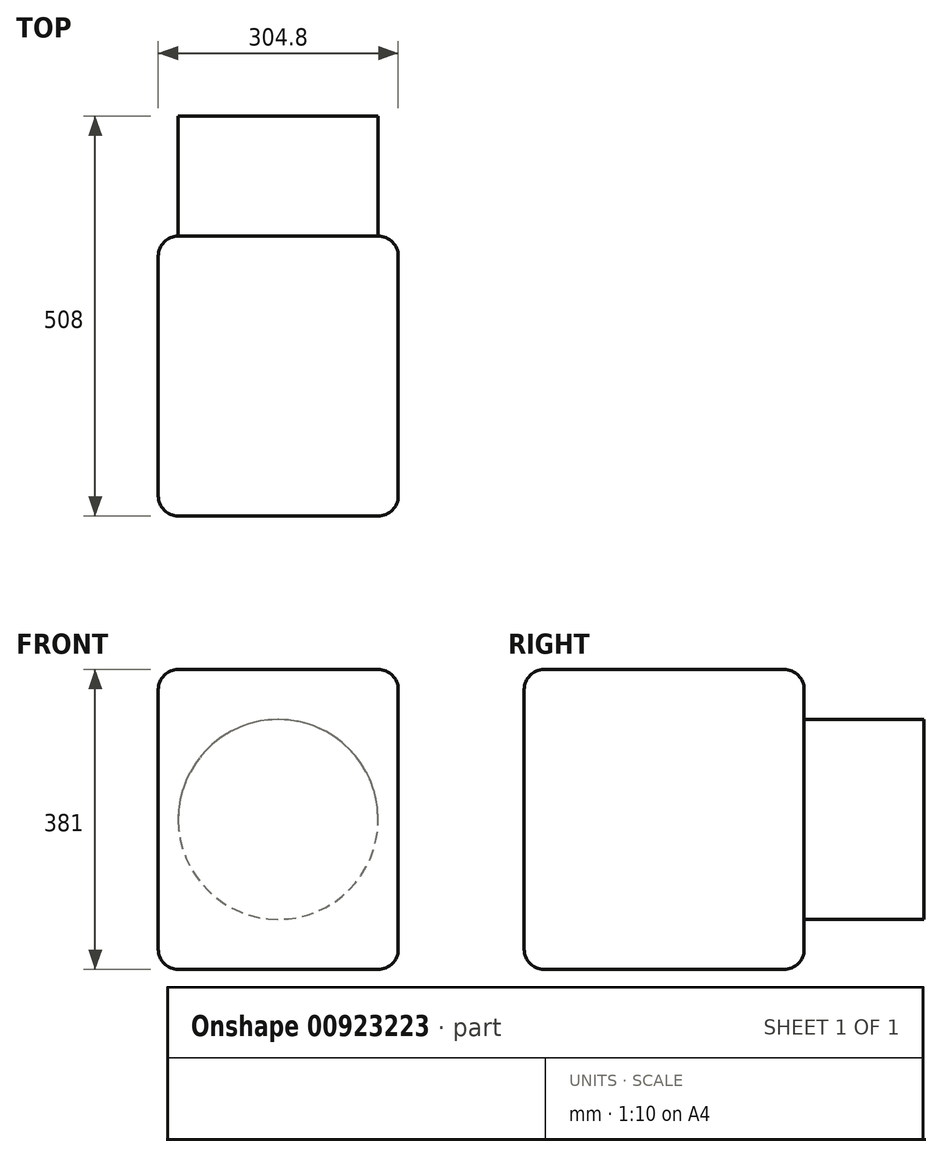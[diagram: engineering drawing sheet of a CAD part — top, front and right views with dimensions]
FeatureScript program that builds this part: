
annotation { "Feature Type Name" : "Feature", "Feature Type Description" : "" }
export const myFeature = defineFeature(function(context is Context, id is Id, definition is map)
    precondition{}
    {
        {
            var Q0;
            Q0=qCreatedBy(makeId("Front.planeOp"),FACE);
            var sketch = newSketch(context, id + "F0", { "sketchPlane" : qUnion([Q0])});
            skLineSegment(sketch, "E0.bottom", {"start": v(152.4, 190.5) * mm, "end": v(-152.4, 190.5) * mm});
            skLineSegment(sketch, "E0.top", {"start": v(152.4, -190.5) * mm, "end": v(-152.4, -190.5) * mm});
            skLineSegment(sketch, "E0.left", {"start": v(152.4, 190.5) * mm, "end": v(152.4, -190.5) * mm});
            skLineSegment(sketch, "E0.right", {"start": v(-152.4, 190.5) * mm, "end": v(-152.4, -190.5) * mm});
            skPoint(sketch, "E0.middle", {"position": v(0, 0) * mm});
            skSolve(sketch);
        }
        {
            var Q0;
            Q0=qSketchRegion(id+"F0",true);
            extrude(context, id + "F1", {"entities" : qUnion([Q0]), "offsetDistance" : 25.4 * mm, "depth" : 355.6 * mm});
        }
        {
            var Q0;
            Q0=makeQuery(id+"F1.opExtrude","CAP_EDGE",EDGE,{"disambiguationData":[OSD([sQuery(id+"F0.wireOp",EDGE,"E0.right")])],"isStart":false});
            var Q1;
            Q1=makeQuery(id+"F1.opExtrude","CAP_EDGE",EDGE,{"disambiguationData":[OSD([sQuery(id+"F0.wireOp",EDGE,"E0.bottom")])],"isStart":false});
            var Q2;
            Q2=makeQuery(id+"F1.opExtrude","CAP_EDGE",EDGE,{"disambiguationData":[OSD([sQuery(id+"F0.wireOp",EDGE,"E0.left")])],"isStart":false});
            var Q3;
            Q3=makeQuery(id+"F1.opExtrude","CAP_EDGE",EDGE,{"disambiguationData":[OSD([sQuery(id+"F0.wireOp",EDGE,"E0.top")])],"isStart":false});
            var Q4;
            Q4=makeQuery(id+"F1.opExtrude","SWEPT_EDGE",EDGE,{"disambiguationData":[OSD([sQuery(id+"F0.wireOp",EDGE,"E0.top"),sQuery(id+"F0.wireOp",EDGE,"E0.right")])]});
            var Q5;
            Q5=makeQuery(id+"F1.opExtrude","SWEPT_EDGE",EDGE,{"disambiguationData":[OSD([sQuery(id+"F0.wireOp",EDGE,"E0.bottom"),sQuery(id+"F0.wireOp",EDGE,"E0.right")])]});
            var Q6;
            Q6=makeQuery(id+"F1.opExtrude","SWEPT_EDGE",EDGE,{"disambiguationData":[OSD([sQuery(id+"F0.wireOp",EDGE,"E0.bottom"),sQuery(id+"F0.wireOp",EDGE,"E0.left")])]});
            var Q7;
            Q7=makeQuery(id+"F1.opExtrude","SWEPT_EDGE",EDGE,{"disambiguationData":[OSD([sQuery(id+"F0.wireOp",EDGE,"E0.top"),sQuery(id+"F0.wireOp",EDGE,"E0.left")])]});
            var Q8;
            Q8=makeQuery(id+"F1.opExtrude","CAP_EDGE",EDGE,{"disambiguationData":[OSD([sQuery(id+"F0.wireOp",EDGE,"E0.top")])],"isStart":true});
            var Q9;
            Q9=makeQuery(id+"F1.opExtrude","CAP_EDGE",EDGE,{"disambiguationData":[OSD([sQuery(id+"F0.wireOp",EDGE,"E0.left")])],"isStart":true});
            var Q10;
            Q10=makeQuery(id+"F1.opExtrude","CAP_EDGE",EDGE,{"disambiguationData":[OSD([sQuery(id+"F0.wireOp",EDGE,"E0.bottom")])],"isStart":true});
            var Q11;
            Q11=makeQuery(id+"F1.opExtrude","CAP_EDGE",EDGE,{"disambiguationData":[OSD([sQuery(id+"F0.wireOp",EDGE,"E0.right")])],"isStart":true});
            fillet(context, id + "F2", {"entities" : qUnion([Q0, Q1, Q2, Q3, Q4, Q5, Q6, Q7, Q8, Q9, Q10, Q11]), "radius" : 25.4 * mm, "tangentPropagation" : true, "allowEdgeOverflow" : false});
        }
        {
            var Q0;
            Q0=makeQuery(id+"F1.opExtrude","CAP_FACE",FACE,{"disambiguationData":[OSD([sQuery(id+"F0.wireOp",EDGE,"E0.bottom"),sQuery(id+"F0.wireOp",EDGE,"E0.top"),sQuery(id+"F0.wireOp",EDGE,"E0.left"),sQuery(id+"F0.wireOp",EDGE,"E0.right")])],"isStart":true});
            var sketch = newSketch(context, id + "F3", { "sketchPlane" : qUnion([Q0])});
            skCircle(sketch, "E1", {"center": v(0, 0) * mm, "radius": 127 * mm});
            skSolve(sketch);
        }
        {
            var Q0;
            Q0 = qSketchRegion(id + "F3", true);
            extrude(context, id + "F4", {"entities" : qUnion([Q0]), "operationType" : NewBodyOperationType.ADD, "depth" : 152.4 * mm, "offsetDistance" : 25.4 * mm});
        }
    });
